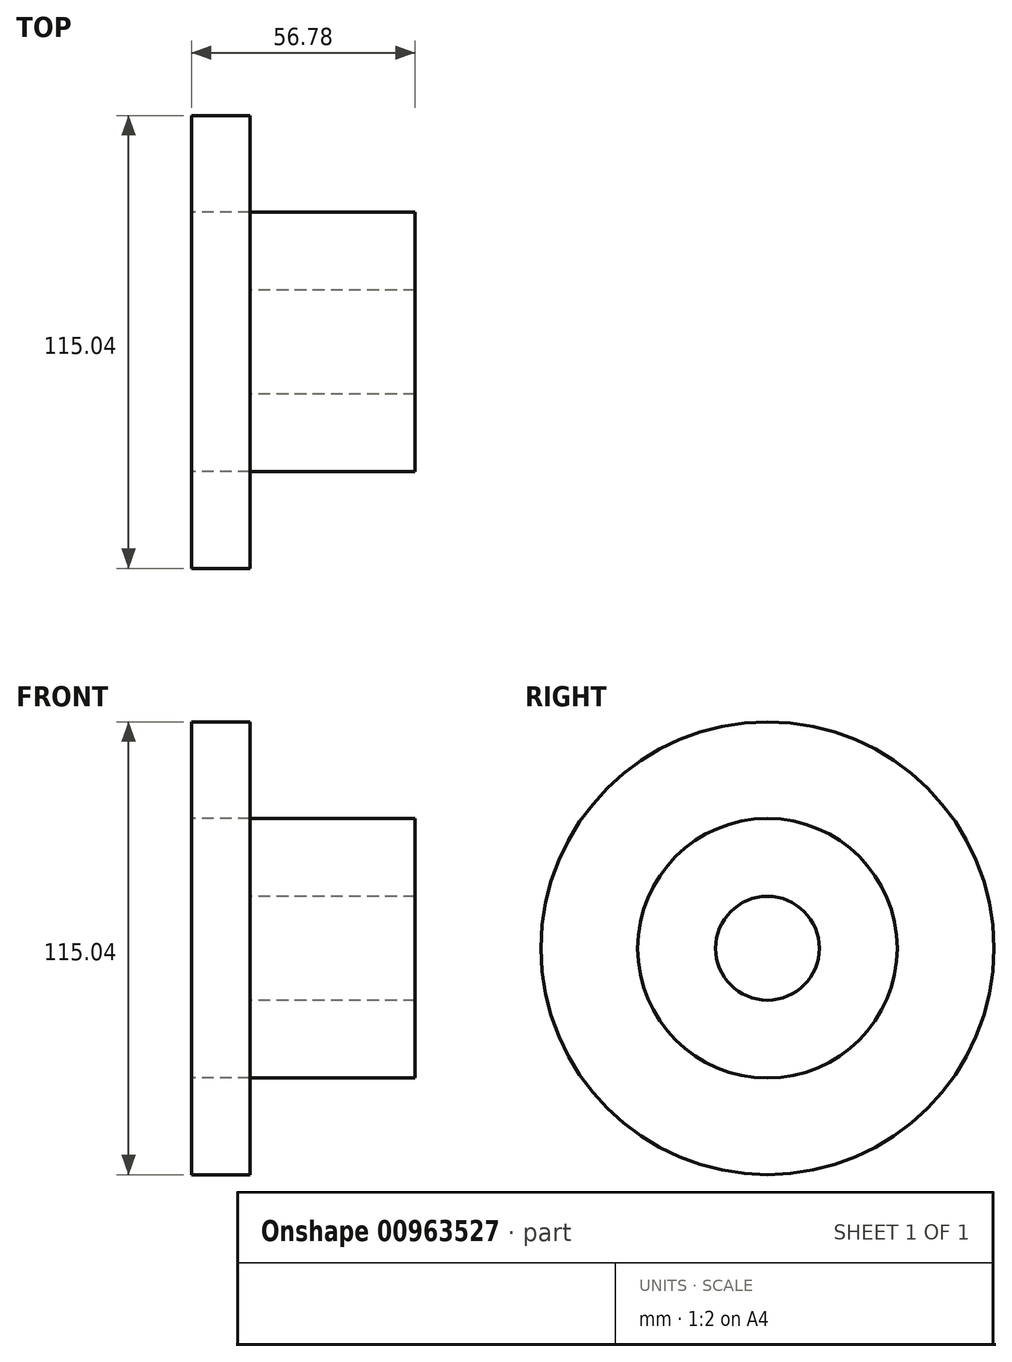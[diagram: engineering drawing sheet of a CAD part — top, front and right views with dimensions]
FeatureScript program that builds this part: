
annotation { "Feature Type Name" : "Feature", "Feature Type Description" : "" }
export const myFeature = defineFeature(function(context is Context, id is Id, definition is map)
    precondition{}
    {
        {
            var Q0;
            Q0=qCreatedBy(makeId("Front.planeOp"),FACE);
            var sketch = newSketch(context, id + "F0", { "sketchPlane" : qUnion([Q0])});
            skLineSegment(sketch, "E0.bottom", {"start": v(-39.28, 57.52) * mm, "end": v(-24.47, 57.52) * mm});
            skLineSegment(sketch, "E0.top", {"start": v(-39.28, 13.2) * mm, "end": v(-24.47, 13.2) * mm});
            skLineSegment(sketch, "E0.left", {"start": v(-39.28, 57.52) * mm, "end": v(-39.28, 13.2) * mm});
            skLineSegment(sketch, "E0.right", {"start": v(-24.47, 57.52) * mm, "end": v(-24.47, 13.2) * mm});
            skLineSegment(sketch, "E1.bottom", {"start": v(-39.28, 13.2) * mm, "end": v(17.5, 13.2) * mm});
            skLineSegment(sketch, "E1.top", {"start": v(-39.28, 32.97) * mm, "end": v(17.5, 32.97) * mm});
            skLineSegment(sketch, "E1.left", {"start": v(-39.28, 13.2) * mm, "end": v(-39.28, 32.97) * mm});
            skLineSegment(sketch, "E1.right", {"start": v(17.5, 13.2) * mm, "end": v(17.5, 32.97) * mm});
            skSolve(sketch);
        }
        {
            var Q0;
            Q0=qCreatedBy(makeId("Front.planeOp"),FACE);
            var sketch = newSketch(context, id + "F1", { "sketchPlane" : qUnion([Q0])});
            skLineSegment(sketch, "E2", {"start": v(-39.28, 0) * mm, "end": v(16.72, 0) * mm});
            skSolve(sketch);
        }
        {
            var Q0;
            {var subQ5=sQuery(id+"F0.wireOp",EDGE,"E1.right");Q0=makeQuery(id+"F0.imprint","IMPRINT",FACE,{"disambiguationData":[TD([[makeQuery(id+"F0.imprint","IMPRINT",EDGE,{"derivedFrom":subQ5}),1.0]])]});}
            var Q1;
            {var subQ0=sQuery(id+"F0.wireOp",EDGE,"E0.bottom");Q1=makeQuery(id+"F0.imprint","IMPRINT",FACE,{"disambiguationData":[TD([[makeQuery(id+"F0.imprint","IMPRINT",EDGE,{"derivedFrom":subQ0}),-1.0]])]});}
            var Q2;
            {var subQ5=sQuery(id+"F0.wireOp",EDGE,"E1.left");Q2=makeQuery(id+"F0.imprint","IMPRINT",FACE,{"disambiguationData":[TD([[makeQuery(id+"F0.imprint","IMPRINT",EDGE,{"derivedFrom":subQ5}),-1.0]])]});}
            var Q3;
            Q3=sQuery(id+"F1.wireOp",EDGE,"E2");
            revolve(context, id + "F2", {"surfaceOperationType" : NewSurfaceOperationType.NEW, "entities" : qUnion([Q0, Q1, Q2]), "axis" : qUnion([Q3]), "revolveType" : RevolveType.FULL});
        }
    });
